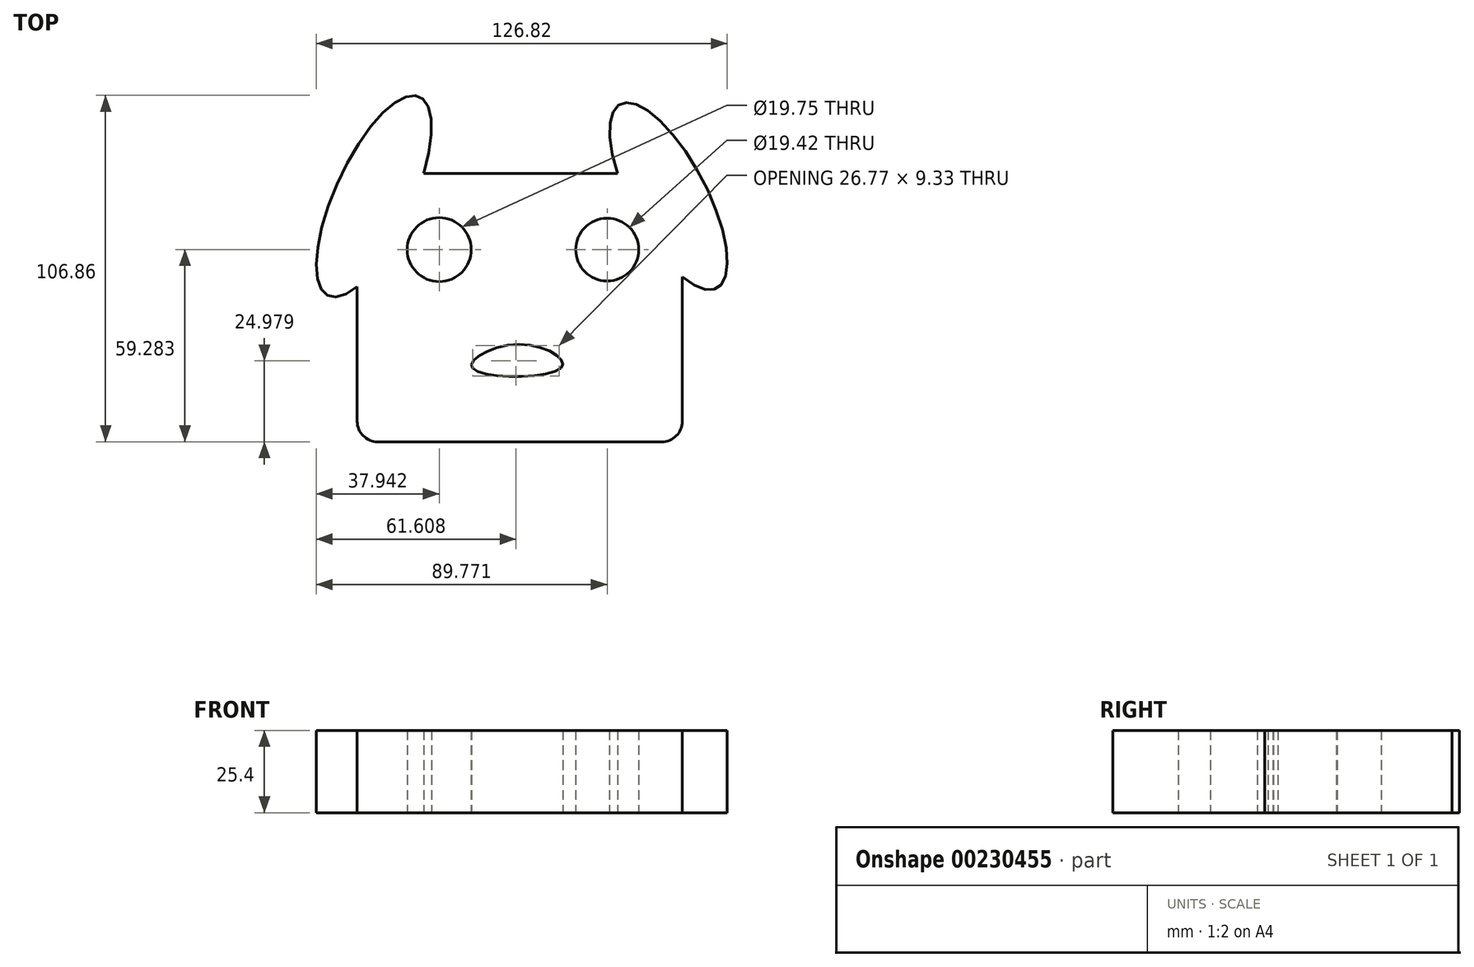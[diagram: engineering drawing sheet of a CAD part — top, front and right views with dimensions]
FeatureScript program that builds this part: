
annotation { "Feature Type Name" : "Feature", "Feature Type Description" : "" }
export const myFeature = defineFeature(function(context is Context, id is Id, definition is map)
    precondition{}
    {
        {
            var Q0;
            Q0=qCreatedBy(makeId("Top.planeOp"),FACE);
            var sketch = newSketch(context, id + "F0", { "sketchPlane" : qUnion([Q0])});
            skLineSegment(sketch, "E0.bottom", {"start": v(-50.35, 52.7) * mm, "end": v(49.93, 52.7) * mm});
            skLineSegment(sketch, "E0.top", {"start": v(-44, -30.08) * mm, "end": v(43.58, -30.08) * mm});
            skLineSegment(sketch, "E0.left", {"start": v(-50.35, 52.7) * mm, "end": v(-50.35, -23.73) * mm});
            skLineSegment(sketch, "E0.right", {"start": v(49.93, 52.7) * mm, "end": v(49.93, -23.73) * mm});
            skCircle(sketch, "E1", {"center": v(-25.06, 29.2) * mm, "radius": 9.87 * mm});
            skCircle(sketch, "E2", {"center": v(26.77, 29.2) * mm, "radius": 9.71 * mm});
            skFitSpline(sketch, "E3", {"points": [v(-14.78, -7.42) * mm, v(0, 0) * mm, v(12.64, -7.2) * mm, v(-14.78, -7.42) * mm]});
            skPoint(sketch, "E4.visualSharp", {"position": v(-50.35, -30.08) * mm});
            skArc(sketch, "E4.filletArc", {"start": v(-50.35, -23.73) * mm, "mid": v(-48.5, -28.22) * mm, "end": v(-44, -30.08) * mm});
            skPoint(sketch, "E5.visualSharp", {"position": v(49.93, -30.08) * mm});
            skArc(sketch, "E5.filletArc", {"start": v(43.58, -30.08) * mm, "mid": v(48.07, -28.22) * mm, "end": v(49.93, -23.73) * mm});
            skSolve(sketch);
        }
        {
            var Q0;
            Q0=makeQuery(id+"F0.imprint","IMPRINT",FACE,{"disambiguationData":[TD([[makeQuery(id+"F0.imprint","IMPRINT",EDGE,{"derivedFrom":sQuery(id+"F0.wireOp",EDGE,"E0.bottom")}),-1.0]])]});
            var sketch = newSketch(context, id + "F1", { "sketchPlane" : qUnion([Q0])});
            skEllipse(sketch, "E6", {"center": v(-45.23, 45.66) * mm, "majorRadius": 33.8 * mm, "minorRadius": 11.91 * mm, "majorAxis": v(-0.42, -0.9)});
            skEllipse(sketch, "E7", {"center": v(45.66, 45.66) * mm, "majorRadius": 32.07 * mm, "minorRadius": 11.68 * mm, "majorAxis": v(0.47, -0.88)});
            skSolve(sketch);
        }
        {
            var Q0;
            Q0=makeQuery(id+"F0.imprint","IMPRINT",FACE,{"disambiguationData":[TD([[makeQuery(id+"F0.imprint","IMPRINT",EDGE,{"derivedFrom":sQuery(id+"F0.wireOp",EDGE,"E0.bottom")}),-1.0]])]});
            extrude(context, id + "F2", {"entities" : qUnion([Q0]), "depth" : 25.4 * mm});
        }
        {
            var Q0;
            {var subQ0=sQuery(id+"F1.wireOp",EDGE,"E7");var subQ1=makeQuery(id+"F0.imprint","IMPRINT",EDGE,{"derivedFrom":sQuery(id+"F0.wireOp",EDGE,"E0.bottom")});var subQ2=makeQuery(id+"F1.imprint","INTERSECT",VERTEX,{"derivedFrom":[subQ1,subQ0]});Q0=makeQuery(id+"F1.imprint","IMPRINT",FACE,{"disambiguationData":[TD([[makeQuery(id+"F1.imprint","IMPRINT",EDGE,{"disambiguationData":[TD([[subQ2,1.0]])],"derivedFrom":subQ0}),1.0]])]});}
            var sketch = newSketch(context, id + "F3", { "sketchPlane" : qUnion([Q0])});
            skSolve(sketch);
        }
        {
            var Q0;
            Q0 = qSketchRegion(id + "F3", true);
            var Q1;
            {var subQ0=sQuery(id+"F1.wireOp",EDGE,"E6");var subQ1=makeQuery(id+"F0.imprint","IMPRINT",EDGE,{"derivedFrom":sQuery(id+"F0.wireOp",EDGE,"E0.bottom")});var subQ2=makeQuery(id+"F1.imprint","INTERSECT",VERTEX,{"derivedFrom":[subQ1,subQ0]});Q1=makeQuery(id+"F1.imprint","IMPRINT",FACE,{"disambiguationData":[TD([[makeQuery(id+"F1.imprint","IMPRINT",EDGE,{"disambiguationData":[TD([[subQ2,-1.0]])],"derivedFrom":subQ0}),1.0]])]});}
            extrude(context, id + "F4", {"entities" : qUnion([Q0, Q1]), "operationType" : NewBodyOperationType.ADD, "depth" : 25.4 * mm});
        }
        {
            var Q0;
            {var subQ0=sQuery(id+"F1.wireOp",EDGE,"E7");var subQ1=makeQuery(id+"F0.imprint","IMPRINT",EDGE,{"derivedFrom":sQuery(id+"F0.wireOp",EDGE,"E0.bottom")});var subQ2=makeQuery(id+"F1.imprint","INTERSECT",VERTEX,{"derivedFrom":[subQ1,subQ0]});Q0=makeQuery(id+"F3.imprint","IMPRINT",FACE,{"disambiguationData":[TD([[makeQuery(id+"F3.imprint","IMPRINT",EDGE,{"derivedFrom":makeQuery(id+"F1.imprint","IMPRINT",EDGE,{"disambiguationData":[TD([[subQ2,1.0]])],"derivedFrom":subQ0})}),1.0]])]});}
            extrude(context, id + "F5", {"entities" : qUnion([Q0]), "operationType" : NewBodyOperationType.ADD, "depth" : 25.4 * mm});
        }
    });
